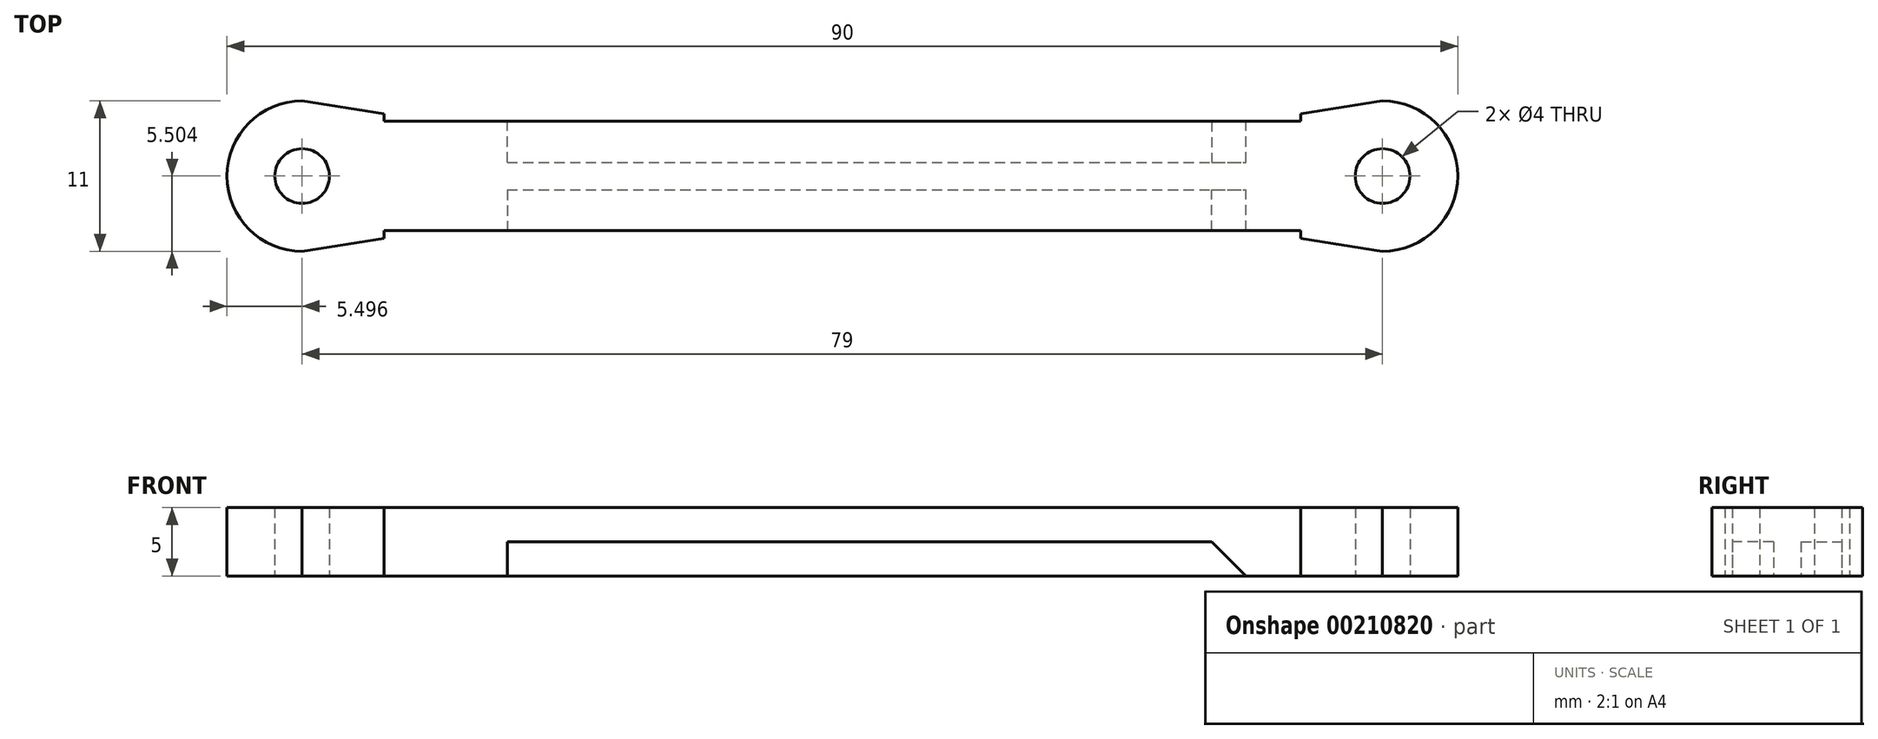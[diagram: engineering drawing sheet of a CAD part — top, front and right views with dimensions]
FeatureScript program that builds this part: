
annotation { "Feature Type Name" : "Feature", "Feature Type Description" : "" }
export const myFeature = defineFeature(function(context is Context, id is Id, definition is map)
    precondition{}
    {
        {
            var Q0;
            Q0=qCreatedBy(makeId("Top.planeOp"),FACE);
            var sketch = newSketch(context, id + "F0", { "sketchPlane" : qUnion([Q0])});
            skLineSegment(sketch, "E0", {"start": v(-53.68, 27.65) * mm, "end": v(6.32, 27.65) * mm});
            skLineSegment(sketch, "E1", {"start": v(-53.68, 19.65) * mm, "end": v(6.32, 19.65) * mm});
            skLineSegment(sketch, "E2", {"start": v(-57.18, 24.65) * mm, "end": v(9.82, 24.65) * mm});
            skLineSegment(sketch, "E3", {"start": v(-57.18, 22.65) * mm, "end": v(9.82, 22.65) * mm});
            skLineSegment(sketch, "E4", {"start": v(-53.68, 27.65) * mm, "end": v(-53.68, 19.65) * mm});
            skLineSegment(sketch, "E5", {"start": v(6.32, 27.65) * mm, "end": v(6.32, 19.65) * mm});
            skLineSegment(sketch, "E6", {"start": v(-57.18, 24.65) * mm, "end": v(-57.18, 22.65) * mm});
            skLineSegment(sketch, "E7", {"start": v(9.82, 24.65) * mm, "end": v(9.82, 22.65) * mm});
            skLineSegment(sketch, "E8", {"start": v(-57.18, 23.65) * mm, "end": v(-63.18, 23.65) * mm});
            skCircle(sketch, "E9", {"center": v(-63.18, 23.65) * mm, "radius": 2 * mm});
            skLineSegment(sketch, "E10", {"start": v(9.82, 23.65) * mm, "end": v(15.82, 23.65) * mm});
            skCircle(sketch, "E11", {"center": v(15.82, 23.65) * mm, "radius": 2 * mm});
            skCircle(sketch, "E12", {"center": v(15.82, 23.65) * mm, "radius": 5.5 * mm});
            skCircle(sketch, "E13", {"center": v(-63.18, 23.65) * mm, "radius": 5.5 * mm});
            skLineSegment(sketch, "E14", {"start": v(-63.18, 23.65) * mm, "end": v(-63.18, 18.15) * mm});
            skLineSegment(sketch, "E15", {"start": v(-63.18, 18.15) * mm, "end": v(-53.68, 19.65) * mm});
            skLineSegment(sketch, "E16", {"start": v(-63.18, 23.65) * mm, "end": v(-63.18, 29.15) * mm});
            skLineSegment(sketch, "E17", {"start": v(-63.18, 29.15) * mm, "end": v(-53.68, 27.65) * mm});
            skLineSegment(sketch, "E18", {"start": v(15.82, 23.65) * mm, "end": v(15.82, 29.15) * mm});
            skLineSegment(sketch, "E19", {"start": v(15.82, 29.15) * mm, "end": v(6.32, 27.65) * mm});
            skLineSegment(sketch, "E20", {"start": v(15.82, 23.65) * mm, "end": v(15.82, 18.15) * mm});
            skLineSegment(sketch, "E21", {"start": v(15.82, 18.15) * mm, "end": v(6.32, 19.65) * mm});
            skLineSegment(sketch, "E22", {"start": v(9.82, 22.65) * mm, "end": v(9.82, 19.1) * mm});
            skLineSegment(sketch, "E23", {"start": v(9.82, 24.65) * mm, "end": v(9.82, 28.2) * mm});
            skLineSegment(sketch, "E24", {"start": v(-57.18, 24.65) * mm, "end": v(-57.18, 28.2) * mm});
            skLineSegment(sketch, "E25", {"start": v(-57.18, 22.65) * mm, "end": v(-57.18, 19.1) * mm});
            skSolve(sketch);
        }
        {
            var Q0;
            {var subQ0=sQuery(id+"F0.wireOp",EDGE,"E18");var subQ1=sQuery(id+"F0.wireOp",EDGE,"E11");var subQ2=makeQuery(id+"F0.imprint","INTERSECT",VERTEX,{"derivedFrom":[subQ1,subQ0]});Q0=makeQuery(id+"F0.imprint","IMPRINT",FACE,{"disambiguationData":[TD([[makeQuery(id+"F0.imprint","IMPRINT",EDGE,{"disambiguationData":[TD([[subQ2,1.0]])],"derivedFrom":subQ1}),-1.0]])]});}
            var Q1;
            {var subQ2=sQuery(id+"F0.wireOp",EDGE,"E12");var subQ6=sQuery(id+"F0.wireOp",EDGE,"E10");var subQ9=makeQuery(id+"F0.imprint","INTERSECT",VERTEX,{"derivedFrom":[subQ6,subQ2]});Q1=makeQuery(id+"F0.imprint","IMPRINT",FACE,{"disambiguationData":[TD([[makeQuery(id+"F0.imprint","IMPRINT",EDGE,{"disambiguationData":[TD([[subQ9,-1.0]])],"derivedFrom":subQ6}),1.0]])]});}
            var Q2;
            {var subQ1=sQuery(id+"F0.wireOp",EDGE,"E12");var subQ3=sQuery(id+"F0.wireOp",EDGE,"E10");var subQ4=makeQuery(id+"F0.imprint","INTERSECT",VERTEX,{"derivedFrom":[subQ3,subQ1]});Q2=makeQuery(id+"F0.imprint","IMPRINT",FACE,{"disambiguationData":[TD([[makeQuery(id+"F0.imprint","IMPRINT",EDGE,{"disambiguationData":[TD([[subQ4,-1.0]])],"derivedFrom":subQ3}),-1.0]])]});}
            var Q3;
            {var subQ7=sQuery(id+"F0.wireOp",EDGE,"E23");Q3=makeQuery(id+"F0.imprint","IMPRINT",FACE,{"disambiguationData":[TD([[makeQuery(id+"F0.imprint","IMPRINT",EDGE,{"derivedFrom":subQ7}),-1.0]])]});}
            var Q4;
            {var subQ0=sQuery(id+"F0.wireOp",EDGE,"E22");Q4=makeQuery(id+"F0.imprint","IMPRINT",FACE,{"disambiguationData":[TD([[makeQuery(id+"F0.imprint","IMPRINT",EDGE,{"derivedFrom":subQ0}),1.0]])]});}
            var Q5;
            {var subQ0=sQuery(id+"F0.wireOp",EDGE,"E4");var subQ1=sQuery(id+"F0.wireOp",EDGE,"E2");var subQ2=makeQuery(id+"F0.imprint","INTERSECT",VERTEX,{"derivedFrom":[subQ1,subQ0]});Q5=makeQuery(id+"F0.imprint","IMPRINT",FACE,{"disambiguationData":[TD([[makeQuery(id+"F0.imprint","IMPRINT",EDGE,{"disambiguationData":[TD([[subQ2,-1.0]])],"derivedFrom":subQ1}),-1.0]])]});}
            var Q6;
            {var subQ1=sQuery(id+"F0.wireOp",EDGE,"E2");var subQ4=sQuery(id+"F0.wireOp",EDGE,"E5");var subQ5=makeQuery(id+"F0.imprint","INTERSECT",VERTEX,{"derivedFrom":[subQ1,subQ4]});Q6=makeQuery(id+"F0.imprint","IMPRINT",FACE,{"disambiguationData":[TD([[makeQuery(id+"F0.imprint","IMPRINT",EDGE,{"disambiguationData":[TD([[subQ5,-1.0]])],"derivedFrom":subQ4}),1.0]])]});}
            var Q7;
            {var subQ2=sQuery(id+"F0.wireOp",EDGE,"E13");var subQ6=sQuery(id+"F0.wireOp",EDGE,"E8");var subQ9=makeQuery(id+"F0.imprint","INTERSECT",VERTEX,{"derivedFrom":[subQ6,subQ2]});Q7=makeQuery(id+"F0.imprint","IMPRINT",FACE,{"disambiguationData":[TD([[makeQuery(id+"F0.imprint","IMPRINT",EDGE,{"disambiguationData":[TD([[subQ9,-1.0]])],"derivedFrom":subQ6}),-1.0]])]});}
            var Q8;
            {var subQ2=sQuery(id+"F0.wireOp",EDGE,"E13");var subQ7=sQuery(id+"F0.wireOp",EDGE,"E8");var subQ8=makeQuery(id+"F0.imprint","INTERSECT",VERTEX,{"derivedFrom":[subQ7,subQ2]});Q8=makeQuery(id+"F0.imprint","IMPRINT",FACE,{"disambiguationData":[TD([[makeQuery(id+"F0.imprint","IMPRINT",EDGE,{"disambiguationData":[TD([[subQ8,-1.0]])],"derivedFrom":subQ7}),1.0]])]});}
            var Q9;
            {var subQ0=sQuery(id+"F0.wireOp",EDGE,"E16");var subQ1=sQuery(id+"F0.wireOp",EDGE,"E9");var subQ2=makeQuery(id+"F0.imprint","INTERSECT",VERTEX,{"derivedFrom":[subQ1,subQ0]});Q9=makeQuery(id+"F0.imprint","IMPRINT",FACE,{"disambiguationData":[TD([[makeQuery(id+"F0.imprint","IMPRINT",EDGE,{"disambiguationData":[TD([[subQ2,-1.0]])],"derivedFrom":subQ1}),-1.0]])]});}
            var Q10;
            {var subQ5=sQuery(id+"F0.wireOp",EDGE,"E24");Q10=makeQuery(id+"F0.imprint","IMPRINT",FACE,{"disambiguationData":[TD([[makeQuery(id+"F0.imprint","IMPRINT",EDGE,{"derivedFrom":subQ5}),1.0]])]});}
            var Q11;
            {var subQ7=sQuery(id+"F0.wireOp",EDGE,"E25");Q11=makeQuery(id+"F0.imprint","IMPRINT",FACE,{"disambiguationData":[TD([[makeQuery(id+"F0.imprint","IMPRINT",EDGE,{"derivedFrom":subQ7}),-1.0]])]});}
            var Q12;
            {var subQ1=sQuery(id+"F0.wireOp",EDGE,"E2");var subQ4=sQuery(id+"F0.wireOp",EDGE,"E4");var subQ5=makeQuery(id+"F0.imprint","INTERSECT",VERTEX,{"derivedFrom":[subQ1,subQ4]});Q12=makeQuery(id+"F0.imprint","IMPRINT",FACE,{"disambiguationData":[TD([[makeQuery(id+"F0.imprint","IMPRINT",EDGE,{"disambiguationData":[TD([[subQ5,-1.0]])],"derivedFrom":subQ4}),-1.0]])]});}
            extrude(context, id + "F1", {"entities" : qUnion([Q0, Q1, Q2, Q3, Q4, Q5, Q6, Q7, Q8, Q9, Q10, Q11, Q12]), "depth" : 5 * mm});
        }
        {
            var Q0;
            Q0=makeQuery(id+"F1.opExtrude","CAP_FACE",FACE,{"disambiguationData":[OSD([sQuery(id+"F0.wireOp",EDGE,"E2"),sQuery(id+"F0.wireOp",EDGE,"E3"),sQuery(id+"F0.wireOp",EDGE,"E9"),sQuery(id+"F0.wireOp",EDGE,"E11"),sQuery(id+"F0.wireOp",EDGE,"E12"),sQuery(id+"F0.wireOp",EDGE,"E13"),sQuery(id+"F0.wireOp",EDGE,"E15"),sQuery(id+"F0.wireOp",EDGE,"E17"),sQuery(id+"F0.wireOp",EDGE,"E19"),sQuery(id+"F0.wireOp",EDGE,"E21"),sQuery(id+"F0.wireOp",EDGE,"E22"),sQuery(id+"F0.wireOp",EDGE,"E23"),sQuery(id+"F0.wireOp",EDGE,"E24"),sQuery(id+"F0.wireOp",EDGE,"E25")])],"isStart":true});
            var sketch = newSketch(context, id + "F2", { "sketchPlane" : qUnion([Q0])});
            skLineSegment(sketch, "E26.bottom", {"start": v(9.82, -22.65) * mm, "end": v(0.82, -22.65) * mm});
            skLineSegment(sketch, "E26.top", {"start": v(9.82, -19.65) * mm, "end": v(0.82, -19.65) * mm});
            skLineSegment(sketch, "E26.left", {"start": v(9.82, -22.65) * mm, "end": v(9.82, -19.65) * mm});
            skLineSegment(sketch, "E26.right", {"start": v(0.82, -22.65) * mm, "end": v(0.82, -19.65) * mm});
            skLineSegment(sketch, "E27.bottom", {"start": v(9.82, -24.65) * mm, "end": v(0.82, -24.65) * mm});
            skLineSegment(sketch, "E27.top", {"start": v(9.82, -27.65) * mm, "end": v(0.82, -27.65) * mm});
            skLineSegment(sketch, "E27.left", {"start": v(9.82, -24.65) * mm, "end": v(9.82, -27.65) * mm});
            skLineSegment(sketch, "E27.right", {"start": v(0.82, -24.65) * mm, "end": v(0.82, -27.65) * mm});
            skLineSegment(sketch, "E28.bottom", {"start": v(-57.18, -22.65) * mm, "end": v(-48.18, -22.65) * mm});
            skLineSegment(sketch, "E28.top", {"start": v(-57.18, -19.65) * mm, "end": v(-48.18, -19.65) * mm});
            skLineSegment(sketch, "E28.left", {"start": v(-57.18, -22.65) * mm, "end": v(-57.18, -19.65) * mm});
            skLineSegment(sketch, "E28.right", {"start": v(-48.18, -22.65) * mm, "end": v(-48.18, -19.65) * mm});
            skLineSegment(sketch, "E29.bottom", {"start": v(-57.18, -24.65) * mm, "end": v(-48.18, -24.65) * mm});
            skLineSegment(sketch, "E29.top", {"start": v(-57.18, -27.65) * mm, "end": v(-48.18, -27.65) * mm});
            skLineSegment(sketch, "E29.left", {"start": v(-57.18, -24.65) * mm, "end": v(-57.18, -27.65) * mm});
            skLineSegment(sketch, "E29.right", {"start": v(-48.18, -24.65) * mm, "end": v(-48.18, -27.65) * mm});
            skSolve(sketch);
        }
        {
            var Q0;
            Q0 = qSketchRegion(id + "F2", true);
            extrude(context, id + "F3", {"entities" : qUnion([Q0]), "operationType" : NewBodyOperationType.ADD, "oppositeDirection" : true, "depth" : 5 * mm});
        }
        {
            var Q0;
            Q0=makeQuery(id+"F3.boolean.opBoolean","MERGE",FACE,{"derivedFrom":[makeQuery(id+"F1.opExtrude","CAP_FACE",FACE,{"disambiguationData":[OSD([sQuery(id+"F0.wireOp",EDGE,"E2"),sQuery(id+"F0.wireOp",EDGE,"E3"),sQuery(id+"F0.wireOp",EDGE,"E9"),sQuery(id+"F0.wireOp",EDGE,"E11"),sQuery(id+"F0.wireOp",EDGE,"E12"),sQuery(id+"F0.wireOp",EDGE,"E13"),sQuery(id+"F0.wireOp",EDGE,"E15"),sQuery(id+"F0.wireOp",EDGE,"E17"),sQuery(id+"F0.wireOp",EDGE,"E19"),sQuery(id+"F0.wireOp",EDGE,"E21"),sQuery(id+"F0.wireOp",EDGE,"E22"),sQuery(id+"F0.wireOp",EDGE,"E23"),sQuery(id+"F0.wireOp",EDGE,"E24"),sQuery(id+"F0.wireOp",EDGE,"E25")])],"isStart":false}),makeQuery(id+"F3.opExtrude","CAP_FACE",FACE,{"disambiguationData":[OSD([sQuery(id+"F2.wireOp",EDGE,"E26.bottom"),sQuery(id+"F2.wireOp",EDGE,"E26.top"),sQuery(id+"F2.wireOp",EDGE,"E26.left"),sQuery(id+"F2.wireOp",EDGE,"E26.right")])],"isStart":false}),makeQuery(id+"F3.opExtrude","CAP_FACE",FACE,{"disambiguationData":[OSD([sQuery(id+"F2.wireOp",EDGE,"E27.bottom"),sQuery(id+"F2.wireOp",EDGE,"E27.top"),sQuery(id+"F2.wireOp",EDGE,"E27.left"),sQuery(id+"F2.wireOp",EDGE,"E27.right")])],"isStart":false}),makeQuery(id+"F3.opExtrude","CAP_FACE",FACE,{"disambiguationData":[OSD([sQuery(id+"F2.wireOp",EDGE,"E28.bottom"),sQuery(id+"F2.wireOp",EDGE,"E28.top"),sQuery(id+"F2.wireOp",EDGE,"E28.left"),sQuery(id+"F2.wireOp",EDGE,"E28.right")])],"isStart":false}),makeQuery(id+"F3.opExtrude","CAP_FACE",FACE,{"disambiguationData":[OSD([sQuery(id+"F2.wireOp",EDGE,"E29.bottom"),sQuery(id+"F2.wireOp",EDGE,"E29.top"),sQuery(id+"F2.wireOp",EDGE,"E29.left"),sQuery(id+"F2.wireOp",EDGE,"E29.right")])],"isStart":false})]});
            var sketch = newSketch(context, id + "F4", { "sketchPlane" : qUnion([Q0])});
            skLineSegment(sketch, "E30", {"start": v(0.82, 27.65) * mm, "end": v(-48.18, 27.65) * mm});
            skLineSegment(sketch, "E31", {"start": v(0.82, 19.65) * mm, "end": v(-48.18, 19.65) * mm});
            skSolve(sketch);
        }
        {
            var Q0;
            Q0 = qSketchRegion(id + "F4", true);
            var Q1;
            Q1=makeQuery(id+"F4.imprint","IMPRINT",FACE,{"disambiguationData":[TD([[makeQuery(id+"F4.imprint","IMPRINT",EDGE,{"derivedFrom":sQuery(id+"F4.wireOp",EDGE,"E31")}),-1.0]])]});
            var Q2;
            Q2=makeQuery(id+"F4.imprint","IMPRINT",FACE,{"disambiguationData":[TD([[makeQuery(id+"F4.imprint","IMPRINT",EDGE,{"derivedFrom":sQuery(id+"F4.wireOp",EDGE,"E30")}),1.0]])]});
            extrude(context, id + "F5", {"entities" : qUnion([Q0, Q1, Q2]), "operationType" : NewBodyOperationType.ADD, "oppositeDirection" : true, "depth" : 2.5 * mm});
        }
        {
            var Q0;
            Q0=makeQuery(id+"F3.opExtrude","CAP_EDGE",EDGE,{"disambiguationData":[OSD([sQuery(id+"F2.wireOp",EDGE,"E26.right")])],"isStart":true});
            var Q1;
            Q1=makeQuery(id+"F3.opExtrude","CAP_EDGE",EDGE,{"disambiguationData":[OSD([sQuery(id+"F2.wireOp",EDGE,"E27.right")])],"isStart":true});
            chamfer(context, id + "F6", {"entities" : qUnion([Q0, Q1]), "width" : 5 * mm, "tangentPropagation" : true});
        }
    });
